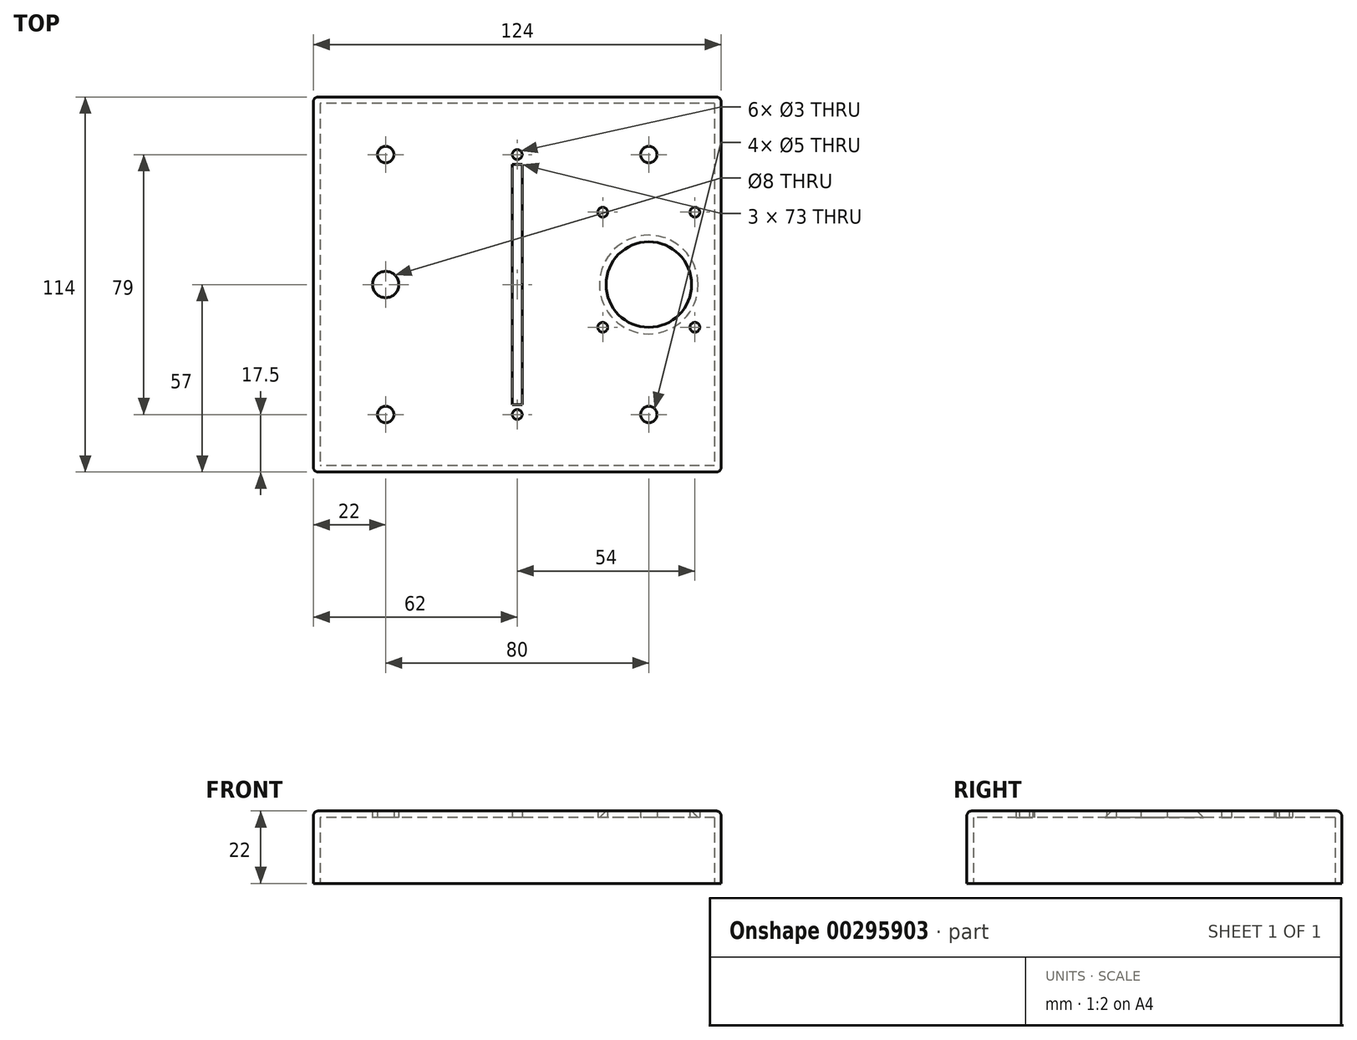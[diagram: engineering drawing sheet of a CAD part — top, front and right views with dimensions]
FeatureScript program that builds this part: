
annotation { "Feature Type Name" : "Feature", "Feature Type Description" : "" }
export const myFeature = defineFeature(function(context is Context, id is Id, definition is map)
    precondition{}
    {
        {
            var Q0;
            Q0=qCreatedBy(makeId("Top.planeOp"),FACE);
            var sketch = newSketch(context, id + "F0", { "sketchPlane" : qUnion([Q0])});
            skCircle(sketch, "E0", {"center": v(40, 0) * mm, "radius": 10 * mm});
            skCircle(sketch, "E1", {"center": v(-40, 0) * mm, "radius": 4 * mm});
            skCircle(sketch, "E2", {"center": v(-40, 39.5) * mm, "radius": 2.5 * mm});
            skCircle(sketch, "E3", {"center": v(0, 39.5) * mm, "radius": 1.5 * mm});
            skCircle(sketch, "E4", {"center": v(40, 39.5) * mm, "radius": 2.5 * mm});
            skLineSegment(sketch, "E5", {"start": v(0, 0) * mm, "end": v(40, 0) * mm, "construction": true});
            skLineSegment(sketch, "E6", {"start": v(-40, 0) * mm, "end": v(0, 0) * mm, "construction": true});
            skLineSegment(sketch, "E7", {"start": v(0, 0) * mm, "end": v(0, 39.5) * mm, "construction": true});
            skLineSegment(sketch, "E8", {"start": v(0, 0) * mm, "end": v(0, -39.5) * mm, "construction": true});
            skCircle(sketch, "E9.MirrorC", {"center": v(0, -39.5) * mm, "radius": 1.5 * mm});
            skLineSegment(sketch, "E10.bottom", {"start": v(1.5, 36.5) * mm, "end": v(-1.5, 36.5) * mm});
            skLineSegment(sketch, "E10.top", {"start": v(1.5, -36.5) * mm, "end": v(-1.5, -36.5) * mm});
            skLineSegment(sketch, "E10.left", {"start": v(1.5, 36.5) * mm, "end": v(1.5, -36.5) * mm});
            skLineSegment(sketch, "E10.right", {"start": v(-1.5, 36.5) * mm, "end": v(-1.5, -36.5) * mm});
            skPoint(sketch, "E10.middle", {"position": v(0, 0) * mm});
            skLineSegment(sketch, "E11.bottom", {"start": v(60, 55) * mm, "end": v(-60, 55) * mm});
            skLineSegment(sketch, "E11.top", {"start": v(60, -55) * mm, "end": v(-60, -55) * mm});
            skLineSegment(sketch, "E11.left", {"start": v(60, 55) * mm, "end": v(60, -55) * mm});
            skLineSegment(sketch, "E11.right", {"start": v(-60, 55) * mm, "end": v(-60, -55) * mm});
            skLineSegment(sketch, "E12", {"start": v(40, 0) * mm, "end": v(40, -13) * mm, "construction": true});
            skLineSegment(sketch, "E13", {"start": v(54, -13) * mm, "end": v(26, -13) * mm, "construction": true});
            skLineSegment(sketch, "E14", {"start": v(26, -13) * mm, "end": v(26, 22) * mm, "construction": true});
            skLineSegment(sketch, "E15", {"start": v(26, 22) * mm, "end": v(54, 22) * mm, "construction": true});
            skLineSegment(sketch, "E16", {"start": v(54, 22) * mm, "end": v(54, -13) * mm, "construction": true});
            skCircle(sketch, "E17", {"center": v(26, 22) * mm, "radius": 1.5 * mm});
            skCircle(sketch, "E18", {"center": v(54, 22) * mm, "radius": 1.5 * mm});
            skCircle(sketch, "E19", {"center": v(54, -13) * mm, "radius": 1.5 * mm});
            skCircle(sketch, "E20", {"center": v(26, -13) * mm, "radius": 1.5 * mm});
            skCircle(sketch, "E21.MirrorC", {"center": v(-40, -39.5) * mm, "radius": 2.5 * mm});
            skCircle(sketch, "E22.MirrorC", {"center": v(40, -39.5) * mm, "radius": 2.5 * mm});
            skCircle(sketch, "E23", {"center": v(283.44, -1.22) * mm, "radius": 10 * mm});
            skCircle(sketch, "E24", {"center": v(203.44, -1.22) * mm, "radius": 4 * mm});
            skCircle(sketch, "E25", {"center": v(203.44, 38.28) * mm, "radius": 2.5 * mm});
            skCircle(sketch, "E26", {"center": v(243.44, 38.28) * mm, "radius": 1.5 * mm});
            skCircle(sketch, "E27", {"center": v(283.44, 38.28) * mm, "radius": 2.5 * mm});
            skLineSegment(sketch, "E28", {"start": v(243.44, -1.22) * mm, "end": v(283.44, -1.22) * mm, "construction": true});
            skLineSegment(sketch, "E29", {"start": v(203.44, -1.22) * mm, "end": v(243.44, -1.22) * mm, "construction": true});
            skLineSegment(sketch, "E30", {"start": v(243.44, -1.22) * mm, "end": v(243.44, 38.28) * mm, "construction": true});
            skLineSegment(sketch, "E31", {"start": v(243.44, -1.22) * mm, "end": v(243.44, -40.72) * mm, "construction": true});
            skCircle(sketch, "E32.MirrorC", {"center": v(243.44, -40.72) * mm, "radius": 1.5 * mm});
            skLineSegment(sketch, "E33.bottom", {"start": v(244.94, 35.28) * mm, "end": v(241.94, 35.28) * mm});
            skLineSegment(sketch, "E33.top", {"start": v(244.94, -37.72) * mm, "end": v(241.94, -37.72) * mm});
            skLineSegment(sketch, "E33.left", {"start": v(244.94, 35.28) * mm, "end": v(244.94, -37.72) * mm});
            skLineSegment(sketch, "E33.right", {"start": v(241.94, 35.28) * mm, "end": v(241.94, -37.72) * mm});
            skPoint(sketch, "E33.middle", {"position": v(243.44, -1.22) * mm});
            skLineSegment(sketch, "E34.bottom", {"start": v(303.44, 53.78) * mm, "end": v(183.44, 53.78) * mm});
            skLineSegment(sketch, "E34.top", {"start": v(303.44, -56.22) * mm, "end": v(183.44, -56.22) * mm});
            skLineSegment(sketch, "E34.left", {"start": v(303.44, 53.78) * mm, "end": v(303.44, -56.22) * mm});
            skLineSegment(sketch, "E34.right", {"start": v(183.44, 53.78) * mm, "end": v(183.44, -56.22) * mm});
            skLineSegment(sketch, "E35", {"start": v(283.44, -1.22) * mm, "end": v(283.44, -14.22) * mm, "construction": true});
            skLineSegment(sketch, "E36", {"start": v(297.44, -14.22) * mm, "end": v(269.44, -14.22) * mm, "construction": true});
            skLineSegment(sketch, "E37", {"start": v(269.44, -14.22) * mm, "end": v(269.44, 20.78) * mm, "construction": true});
            skLineSegment(sketch, "E38", {"start": v(269.44, 20.78) * mm, "end": v(297.44, 20.78) * mm, "construction": true});
            skLineSegment(sketch, "E39", {"start": v(297.44, 20.78) * mm, "end": v(297.44, -14.22) * mm, "construction": true});
            skCircle(sketch, "E40", {"center": v(269.44, 20.78) * mm, "radius": 1.5 * mm});
            skCircle(sketch, "E41", {"center": v(297.44, 20.78) * mm, "radius": 1.5 * mm});
            skCircle(sketch, "E42", {"center": v(297.44, -14.22) * mm, "radius": 1.5 * mm});
            skCircle(sketch, "E43", {"center": v(269.44, -14.22) * mm, "radius": 1.5 * mm});
            skCircle(sketch, "E44.MirrorC", {"center": v(203.44, -40.72) * mm, "radius": 2.5 * mm});
            skCircle(sketch, "E45.MirrorC", {"center": v(283.44, -40.72) * mm, "radius": 2.5 * mm});
            skCircle(sketch, "E46", {"center": v(40, 0) * mm, "radius": 13 * mm, "construction": true});
            skSolve(sketch);
        }
        {
            var Q0;
            Q0=makeQuery(id+"F0.imprint","IMPRINT",FACE,{"disambiguationData":[TD([[makeQuery(id+"F0.imprint","IMPRINT",EDGE,{"derivedFrom":sQuery(id+"F0.wireOp",EDGE,"E0")}),-1.0]])]});
            extrude(context, id + "F1", {"entities" : qUnion([Q0]), "depth" : 2 * mm, "offsetDistance" : 25 * mm});
        }
        {
            var Q0;
            Q0=makeQuery(id+"F1.opExtrude","CAP_FACE",FACE,{"disambiguationData":[OSD([sQuery(id+"F0.wireOp",EDGE,"E0"),sQuery(id+"F0.wireOp",EDGE,"E1"),sQuery(id+"F0.wireOp",EDGE,"E2"),sQuery(id+"F0.wireOp",EDGE,"E3"),sQuery(id+"F0.wireOp",EDGE,"E4"),sQuery(id+"F0.wireOp",EDGE,"E9.MirrorC"),sQuery(id+"F0.wireOp",EDGE,"E10.bottom"),sQuery(id+"F0.wireOp",EDGE,"E10.top"),sQuery(id+"F0.wireOp",EDGE,"E10.left"),sQuery(id+"F0.wireOp",EDGE,"E10.right"),sQuery(id+"F0.wireOp",EDGE,"E11.bottom"),sQuery(id+"F0.wireOp",EDGE,"E11.top"),sQuery(id+"F0.wireOp",EDGE,"E11.left"),sQuery(id+"F0.wireOp",EDGE,"E11.right"),sQuery(id+"F0.wireOp",EDGE,"E17"),sQuery(id+"F0.wireOp",EDGE,"E18"),sQuery(id+"F0.wireOp",EDGE,"E19"),sQuery(id+"F0.wireOp",EDGE,"E20"),sQuery(id+"F0.wireOp",EDGE,"E21.MirrorC"),sQuery(id+"F0.wireOp",EDGE,"E22.MirrorC")])],"isStart":true});
            var Q1;
            Q1=makeQuery(id+"F1.opExtrude","SWEPT_FACE",FACE,{"disambiguationData":[OSD([sQuery(id+"F0.wireOp",EDGE,"E2")])]});
            var Q2;
            Q2=makeQuery(id+"F1.opExtrude","SWEPT_FACE",FACE,{"disambiguationData":[OSD([sQuery(id+"F0.wireOp",EDGE,"E1")])]});
            var Q3;
            Q3=makeQuery(id+"F1.opExtrude","SWEPT_FACE",FACE,{"disambiguationData":[OSD([sQuery(id+"F0.wireOp",EDGE,"E9.MirrorC")])]});
            var Q4;
            Q4=makeQuery(id+"F1.opExtrude","SWEPT_FACE",FACE,{"disambiguationData":[OSD([sQuery(id+"F0.wireOp",EDGE,"E20")])]});
            var Q5;
            Q5=makeQuery(id+"F1.opExtrude","SWEPT_FACE",FACE,{"disambiguationData":[OSD([sQuery(id+"F0.wireOp",EDGE,"E22.MirrorC")])]});
            var Q6;
            Q6=makeQuery(id+"F1.opExtrude","SWEPT_FACE",FACE,{"disambiguationData":[OSD([sQuery(id+"F0.wireOp",EDGE,"E19")])]});
            var Q7;
            Q7=makeQuery(id+"F1.opExtrude","SWEPT_FACE",FACE,{"disambiguationData":[OSD([sQuery(id+"F0.wireOp",EDGE,"E18")])]});
            var Q8;
            Q8=makeQuery(id+"F1.opExtrude","SWEPT_FACE",FACE,{"disambiguationData":[OSD([sQuery(id+"F0.wireOp",EDGE,"E0")])]});
            var Q9;
            Q9=makeQuery(id+"F1.opExtrude","SWEPT_FACE",FACE,{"disambiguationData":[OSD([sQuery(id+"F0.wireOp",EDGE,"E4")])]});
            var Q10;
            Q10=makeQuery(id+"F1.opExtrude","SWEPT_FACE",FACE,{"disambiguationData":[OSD([sQuery(id+"F0.wireOp",EDGE,"E17")])]});
            var Q11;
            Q11=makeQuery(id+"F1.opExtrude","SWEPT_FACE",FACE,{"disambiguationData":[OSD([sQuery(id+"F0.wireOp",EDGE,"E10.bottom")])]});
            var Q12;
            Q12=makeQuery(id+"F1.opExtrude","SWEPT_FACE",FACE,{"disambiguationData":[OSD([sQuery(id+"F0.wireOp",EDGE,"E3")])]});
            var Q13;
            Q13=makeQuery(id+"F1.opExtrude","SWEPT_FACE",FACE,{"disambiguationData":[OSD([sQuery(id+"F0.wireOp",EDGE,"E10.left")])]});
            var Q14;
            Q14=makeQuery(id+"F1.opExtrude","SWEPT_FACE",FACE,{"disambiguationData":[OSD([sQuery(id+"F0.wireOp",EDGE,"E10.right")])]});
            var Q15;
            Q15=makeQuery(id+"F1.opExtrude","SWEPT_FACE",FACE,{"disambiguationData":[OSD([sQuery(id+"F0.wireOp",EDGE,"E10.top")])]});
            var Q16;
            Q16=makeQuery(id+"F1.opExtrude","SWEPT_FACE",FACE,{"disambiguationData":[OSD([sQuery(id+"F0.wireOp",EDGE,"E21.MirrorC")])]});
            shell(context, id + "F2", {"entities" : qUnion([Q0, Q1, Q2, Q3, Q4, Q5, Q6, Q7, Q8, Q9, Q10, Q11, Q12, Q13, Q14, Q15, Q16]), "thickness" : 2 * mm, "oppositeDirection" : true});
        }
        {
            var Q0;
            Q0=makeQuery(id+"F1.opExtrude","CAP_FACE",FACE,{"disambiguationData":[OSD([sQuery(id+"F0.wireOp",EDGE,"E0"),sQuery(id+"F0.wireOp",EDGE,"E1"),sQuery(id+"F0.wireOp",EDGE,"E2"),sQuery(id+"F0.wireOp",EDGE,"E3"),sQuery(id+"F0.wireOp",EDGE,"E4"),sQuery(id+"F0.wireOp",EDGE,"E9.MirrorC"),sQuery(id+"F0.wireOp",EDGE,"E10.bottom"),sQuery(id+"F0.wireOp",EDGE,"E10.top"),sQuery(id+"F0.wireOp",EDGE,"E10.left"),sQuery(id+"F0.wireOp",EDGE,"E10.right"),sQuery(id+"F0.wireOp",EDGE,"E11.bottom"),sQuery(id+"F0.wireOp",EDGE,"E11.top"),sQuery(id+"F0.wireOp",EDGE,"E11.left"),sQuery(id+"F0.wireOp",EDGE,"E11.right"),sQuery(id+"F0.wireOp",EDGE,"E17"),sQuery(id+"F0.wireOp",EDGE,"E18"),sQuery(id+"F0.wireOp",EDGE,"E19"),sQuery(id+"F0.wireOp",EDGE,"E20"),sQuery(id+"F0.wireOp",EDGE,"E21.MirrorC"),sQuery(id+"F0.wireOp",EDGE,"E22.MirrorC")])],"isStart":true});
            extrude(context, id + "F3", {"entities" : qUnion([Q0]), "operationType" : NewBodyOperationType.ADD, "depth" : 18 * mm, "offsetDistance" : 25 * mm});
        }
        {
            var Q0;
            Q0=makeQuery(id+"F1.opExtrude","CAP_EDGE",EDGE,{"disambiguationData":[OSD([sQuery(id+"F0.wireOp",EDGE,"E11.left")])],"isStart":false});
            var Q1;
            Q1=makeQuery(id+"F1.opExtrude","CAP_EDGE",EDGE,{"disambiguationData":[OSD([sQuery(id+"F0.wireOp",EDGE,"E11.bottom")])],"isStart":false});
            var Q2;
            Q2=makeQuery(id+"F1.opExtrude","CAP_EDGE",EDGE,{"disambiguationData":[OSD([sQuery(id+"F0.wireOp",EDGE,"E11.top")])],"isStart":false});
            var Q3;
            Q3=makeQuery(id+"F1.opExtrude","CAP_EDGE",EDGE,{"disambiguationData":[OSD([sQuery(id+"F0.wireOp",EDGE,"E11.right")])],"isStart":false});
            var Q4;
            {var subQ0=sQuery(id+"F0.wireOp",EDGE,"E11.left");var subQ1=sQuery(id+"F0.wireOp",EDGE,"E11.top");Q4=makeQuery(id+"F3.boolean.opBoolean","MERGE",EDGE,{"derivedFrom":[makeQuery(id+"F1.opExtrude","SWEPT_EDGE",EDGE,{"disambiguationData":[OSD([subQ1,subQ0])]}),makeQuery(id+"F3.opExtrude","SWEPT_EDGE",EDGE,{"disambiguationData":[OSD([subQ1,subQ0]),TDD([makeQuery(id+"F1.opExtrude","CAP_VERTEX",VERTEX,{"disambiguationData":[OSD([subQ1,subQ0])],"isStart":true})])]})]});}
            var Q5;
            {var subQ0=sQuery(id+"F0.wireOp",EDGE,"E11.left");var subQ1=sQuery(id+"F0.wireOp",EDGE,"E11.bottom");Q5=makeQuery(id+"F3.boolean.opBoolean","MERGE",EDGE,{"derivedFrom":[makeQuery(id+"F1.opExtrude","SWEPT_EDGE",EDGE,{"disambiguationData":[OSD([subQ1,subQ0])]}),makeQuery(id+"F3.opExtrude","SWEPT_EDGE",EDGE,{"disambiguationData":[OSD([subQ1,subQ0]),TDD([makeQuery(id+"F1.opExtrude","CAP_VERTEX",VERTEX,{"disambiguationData":[OSD([subQ1,subQ0])],"isStart":true})])]})]});}
            var Q6;
            {var subQ0=sQuery(id+"F0.wireOp",EDGE,"E11.right");var subQ1=sQuery(id+"F0.wireOp",EDGE,"E11.bottom");Q6=makeQuery(id+"F3.boolean.opBoolean","MERGE",EDGE,{"derivedFrom":[makeQuery(id+"F1.opExtrude","SWEPT_EDGE",EDGE,{"disambiguationData":[OSD([subQ1,subQ0])]}),makeQuery(id+"F3.opExtrude","SWEPT_EDGE",EDGE,{"disambiguationData":[OSD([subQ1,subQ0]),TDD([makeQuery(id+"F1.opExtrude","CAP_VERTEX",VERTEX,{"disambiguationData":[OSD([subQ1,subQ0])],"isStart":true})])]})]});}
            var Q7;
            {var subQ0=sQuery(id+"F0.wireOp",EDGE,"E11.right");var subQ1=sQuery(id+"F0.wireOp",EDGE,"E11.top");Q7=makeQuery(id+"F3.boolean.opBoolean","MERGE",EDGE,{"derivedFrom":[makeQuery(id+"F1.opExtrude","SWEPT_EDGE",EDGE,{"disambiguationData":[OSD([subQ1,subQ0])]}),makeQuery(id+"F3.opExtrude","SWEPT_EDGE",EDGE,{"disambiguationData":[OSD([subQ1,subQ0]),TDD([makeQuery(id+"F1.opExtrude","CAP_VERTEX",VERTEX,{"disambiguationData":[OSD([subQ1,subQ0])],"isStart":true})])]})]});}
            fillet(context, id + "F4", {"entities" : qUnion([Q0, Q1, Q2, Q3, Q4, Q5, Q6, Q7]), "radius" : 1.5 * mm, "tangentPropagation" : true, "allowEdgeOverflow" : false});
        }
        {
            var Q0;
            Q0=makeQuery(id+"F2.opShell","OFFSET_EDGE",EDGE,{"disambiguationData":[OSD([sQuery(id+"F0.wireOp",EDGE,"E0")])]});
            chamfer(context, id + "F5", {"entities" : qUnion([Q0]), "width" : 5 * mm, "tangentPropagation" : true});
        }
    });
